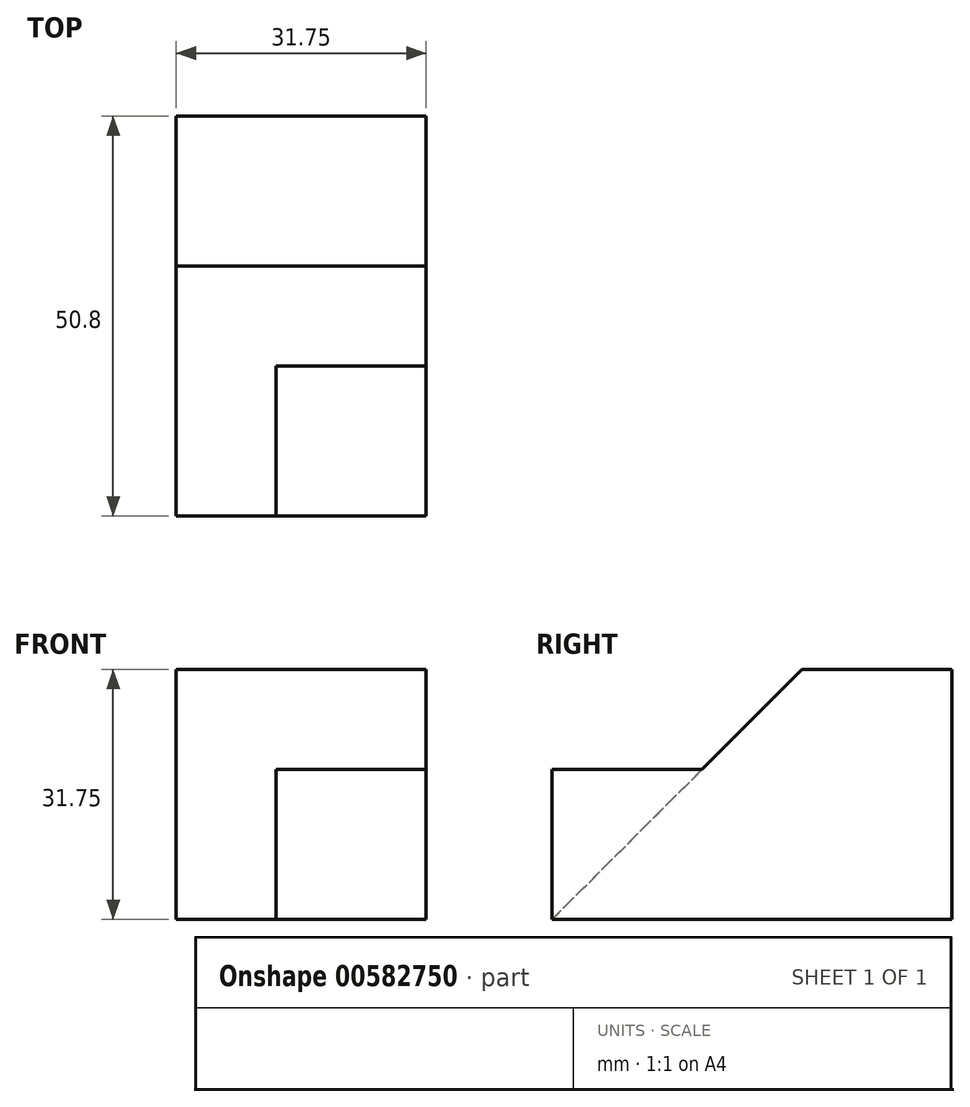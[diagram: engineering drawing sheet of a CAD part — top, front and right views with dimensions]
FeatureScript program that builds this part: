
annotation { "Feature Type Name" : "Feature", "Feature Type Description" : "" }
export const myFeature = defineFeature(function(context is Context, id is Id, definition is map)
    precondition{}
    {
        {
            var Q0;
            Q0=qCreatedBy(makeId("Right.planeOp"),FACE);
            var sketch = newSketch(context, id + "F0", { "sketchPlane" : qUnion([Q0])});
            skLineSegment(sketch, "E0", {"start": v(66.3, 48.5) * mm, "end": v(66.3, 16.74) * mm});
            skLineSegment(sketch, "E1", {"start": v(66.3, 16.74) * mm, "end": v(15.5, 16.74) * mm});
            skLineSegment(sketch, "E2", {"start": v(15.5, 16.74) * mm, "end": v(15.5, 50.61) * mm});
            skLineSegment(sketch, "E3", {"start": v(66.3, 48.5) * mm, "end": v(15.5, 48.5) * mm});
            skSolve(sketch);
        }
        {
            var Q0;
            Q0=makeQuery(id+"F0.imprint","IMPRINT",FACE,{"disambiguationData":[TD([[makeQuery(id+"F0.imprint","IMPRINT",EDGE,{"derivedFrom":sQuery(id+"F0.wireOp",EDGE,"E0")}),-1.0]])]});
            extrude(context, id + "F1", {"entities" : qUnion([Q0]), "depth" : 31.75 * mm, "offsetDistance" : 25.4 * mm});
        }
        {
            var Q0;
            Q0=makeQuery(id+"F1.opExtrude","CAP_FACE",FACE,{"disambiguationData":[OSD([sQuery(id+"F0.wireOp",EDGE,"E0"),sQuery(id+"F0.wireOp",EDGE,"E1"),sQuery(id+"F0.wireOp",EDGE,"E2"),sQuery(id+"F0.wireOp",EDGE,"E3")])],"isStart":true});
            var sketch = newSketch(context, id + "F2", { "sketchPlane" : qUnion([Q0])});
            skLineSegment(sketch, "E4", {"start": v(-47.26, 48.5) * mm, "end": v(-15.5, 16.74) * mm});
            skSolve(sketch);
        }
        {
            var Q0;
            Q0 = qSketchRegion(id + "F2", true);
            var Q1;
            {var subQ0=sQuery(id+"F2.wireOp",EDGE,"E4");Q1=makeQuery(id+"F2.imprint","IMPRINT",FACE,{"disambiguationData":[TD([[makeQuery(id+"F2.imprint","IMPRINT",EDGE,{"derivedFrom":subQ0}),1.0]])]});}
            extrude(context, id + "F3", {"entities" : qUnion([Q0, Q1]), "operationType" : NewBodyOperationType.REMOVE, "oppositeDirection" : true, "depth" : 12.7 * mm, "offsetDistance" : 25.4 * mm});
        }
        {
            var Q0;
            Q0=makeQuery(id+"F3.boolean.opBoolean","COPY",FACE,{"derivedFrom":makeQuery(id+"F3.opExtrude","CAP_FACE",FACE,{"disambiguationData":[OSD([sQuery(id+"F0.wireOp",EDGE,"E2"),sQuery(id+"F0.wireOp",EDGE,"E3"),sQuery(id+"F2.wireOp",EDGE,"E4")])],"isStart":false})});
            var sketch = newSketch(context, id + "F4", { "sketchPlane" : qUnion([Q0])});
            skLineSegment(sketch, "E5", {"start": v(-34.56, 35.8) * mm, "end": v(-15.5, 35.8) * mm});
            skSolve(sketch);
        }
        {
            var Q0;
            Q0 = qSketchRegion(id + "F4", true);
            var Q1;
            {var subQ0=sQuery(id+"F4.wireOp",EDGE,"E5");Q1=makeQuery(id+"F4.imprint","IMPRINT",FACE,{"disambiguationData":[TD([[makeQuery(id+"F4.imprint","IMPRINT",EDGE,{"derivedFrom":subQ0}),1.0]])]});}
            extrude(context, id + "F5", {"entities" : qUnion([Q0, Q1]), "operationType" : NewBodyOperationType.REMOVE, "oppositeDirection" : true, "depth" : 25.4 * mm, "offsetDistance" : 25.4 * mm});
        }
    });
